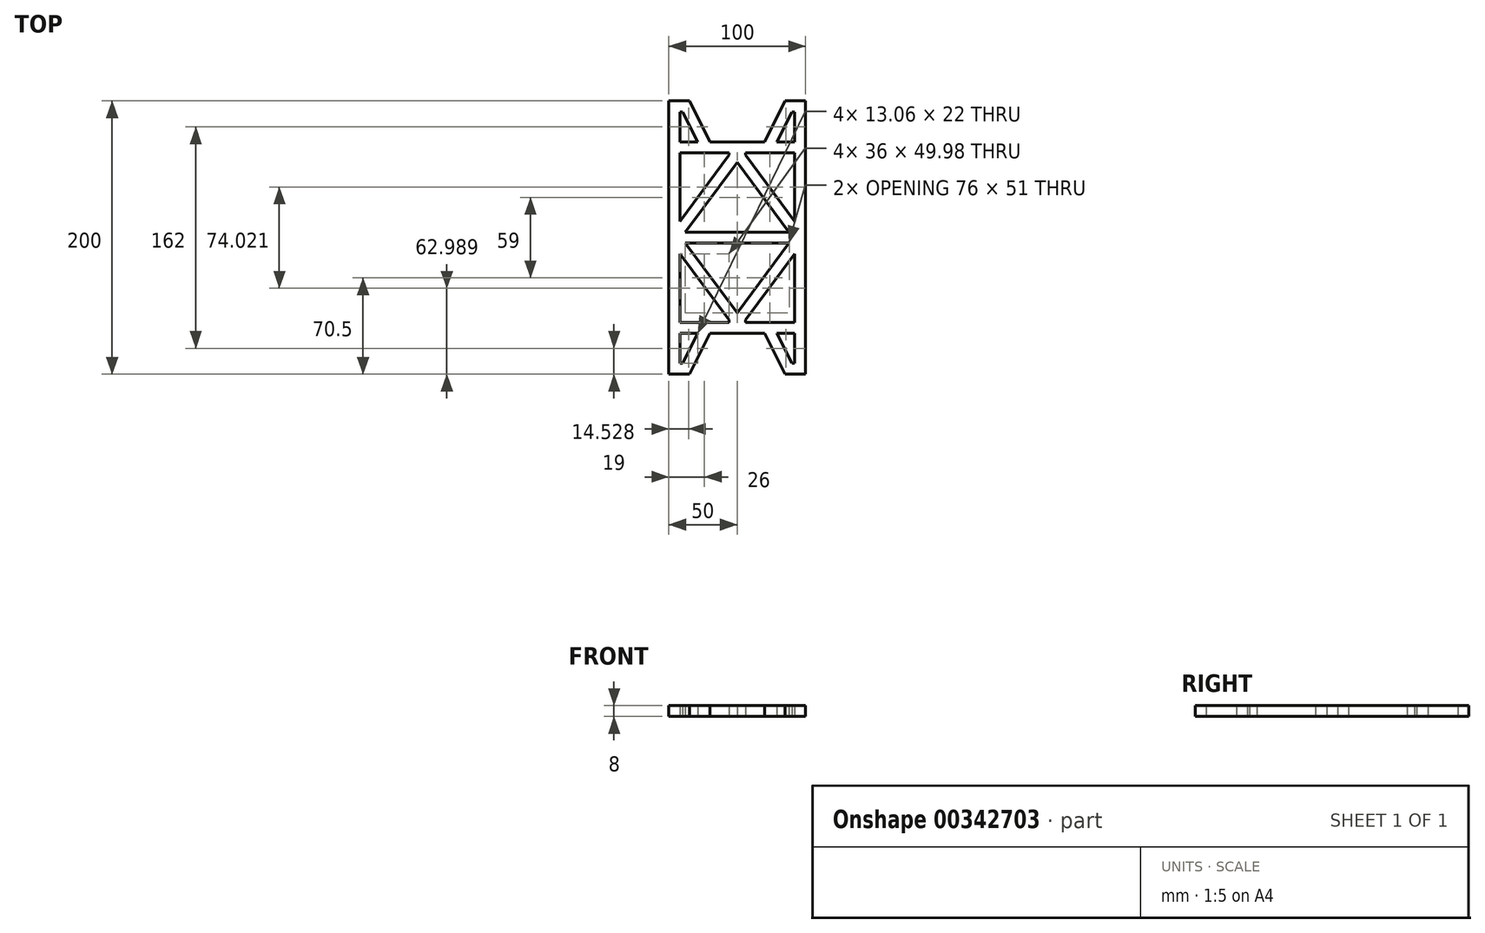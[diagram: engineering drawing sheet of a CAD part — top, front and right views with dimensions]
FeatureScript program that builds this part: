
annotation { "Feature Type Name" : "Feature", "Feature Type Description" : "" }
export const myFeature = defineFeature(function(context is Context, id is Id, definition is map)
    precondition{}
    {
        {
            var Q0;
            Q0=qCreatedBy(makeId("Top.planeOp"),FACE);
            var sketch = newSketch(context, id + "F0", { "sketchPlane" : qUnion([Q0])});
            skLineSegment(sketch, "E0.bottom", {"start": v(-50, 100) * mm, "end": v(0, 100) * mm, "construction": true});
            skLineSegment(sketch, "E0.top", {"start": v(-50, 0) * mm, "end": v(0, 0) * mm, "construction": true});
            skLineSegment(sketch, "E0.left", {"start": v(-50, 100) * mm, "end": v(-50, 0) * mm, "construction": true});
            skLineSegment(sketch, "E0.right", {"start": v(0, 100) * mm, "end": v(0, 0) * mm, "construction": true});
            skLineSegment(sketch, "E1", {"start": v(-50, 0) * mm, "end": v(-50, 100) * mm});
            skLineSegment(sketch, "E2", {"start": v(-50, 100) * mm, "end": v(-35, 100) * mm});
            skLineSegment(sketch, "E3", {"start": v(-35, 100) * mm, "end": v(-20, 70) * mm});
            skLineSegment(sketch, "E4", {"start": v(-20, 70) * mm, "end": v(0, 70) * mm});
            skLineSegment(sketch, "E5", {"start": v(0, 70) * mm, "end": v(0, 55) * mm});
            skLineSegment(sketch, "E6", {"start": v(0, 55) * mm, "end": v(-38, 4) * mm});
            skLineSegment(sketch, "E7.0", {"start": v(-39.94, 92) * mm, "end": v(-28.94, 70) * mm});
            skLineSegment(sketch, "E7.1", {"start": v(-42, 92) * mm, "end": v(-39.94, 92) * mm});
            skLineSegment(sketch, "E7.2", {"start": v(-42, 70) * mm, "end": v(-42, 92) * mm});
            skLineSegment(sketch, "E8.0", {"start": v(-6, 60.34) * mm, "end": v(-42, 12.02) * mm});
            skLineSegment(sketch, "E9", {"start": v(-6, 60.34) * mm, "end": v(-6, 62) * mm});
            skLineSegment(sketch, "E10", {"start": v(-6, 62) * mm, "end": v(-42, 62) * mm});
            skLineSegment(sketch, "E11", {"start": v(-42, 70) * mm, "end": v(-28.94, 70) * mm});
            skLineSegment(sketch, "E12", {"start": v(-42, 62) * mm, "end": v(-42, 12.02) * mm});
            skLineSegment(sketch, "E13", {"start": v(-38, 4) * mm, "end": v(0, 4) * mm});
            skLineSegment(sketch, "E14.MirrorCS", {"start": v(-50, 0) * mm, "end": v(-50, -100) * mm});
            skLineSegment(sketch, "E15.MirrorCS", {"start": v(-50, -100) * mm, "end": v(-35, -100) * mm});
            skLineSegment(sketch, "E16.MirrorCS", {"start": v(-20, -70) * mm, "end": v(0, -70) * mm});
            skLineSegment(sketch, "E17.MirrorCS", {"start": v(-38, -4) * mm, "end": v(0, -4) * mm});
            skLineSegment(sketch, "E18.MirrorCS", {"start": v(0, -55) * mm, "end": v(-38, -4) * mm});
            skLineSegment(sketch, "E19.MirrorCS", {"start": v(-42, -92) * mm, "end": v(-39.94, -92) * mm});
            skLineSegment(sketch, "E20.MirrorCS", {"start": v(-6, -60.34) * mm, "end": v(-6, -62) * mm});
            skLineSegment(sketch, "E21.MirrorCS", {"start": v(-6, -60.34) * mm, "end": v(-42, -12.02) * mm});
            skLineSegment(sketch, "E22.MirrorCS", {"start": v(-42, -70) * mm, "end": v(-28.94, -70) * mm});
            skLineSegment(sketch, "E23.MirrorCS", {"start": v(-6, -62) * mm, "end": v(-42, -62) * mm});
            skLineSegment(sketch, "E24.MirrorCS", {"start": v(-42, -70) * mm, "end": v(-42, -92) * mm});
            skLineSegment(sketch, "E25.MirrorCS", {"start": v(-39.94, -92) * mm, "end": v(-28.94, -70) * mm});
            skLineSegment(sketch, "E26.MirrorCS", {"start": v(-35, -100) * mm, "end": v(-20, -70) * mm});
            skLineSegment(sketch, "E27.MirrorCS", {"start": v(-42, -62) * mm, "end": v(-42, -12.02) * mm});
            skLineSegment(sketch, "E28.MirrorCS", {"start": v(42, -92) * mm, "end": v(39.94, -92) * mm});
            skLineSegment(sketch, "E29.MirrorCS", {"start": v(6, -60.34) * mm, "end": v(6, -62) * mm});
            skLineSegment(sketch, "E30.MirrorCS", {"start": v(6, -60.34) * mm, "end": v(42, -12.02) * mm});
            skLineSegment(sketch, "E31.MirrorCS", {"start": v(50, 0) * mm, "end": v(50, -100) * mm});
            skLineSegment(sketch, "E32.MirrorCS", {"start": v(42, -70) * mm, "end": v(28.94, -70) * mm});
            skLineSegment(sketch, "E33.MirrorCS", {"start": v(0, -55) * mm, "end": v(38, -4) * mm});
            skLineSegment(sketch, "E34.MirrorCS", {"start": v(50, -100) * mm, "end": v(35, -100) * mm});
            skLineSegment(sketch, "E35.MirrorCS", {"start": v(42, -70) * mm, "end": v(42, -92) * mm});
            skLineSegment(sketch, "E36.MirrorCS", {"start": v(42, -62) * mm, "end": v(42, -12.02) * mm});
            skLineSegment(sketch, "E37.MirrorCS", {"start": v(35, -100) * mm, "end": v(20, -70) * mm});
            skLineSegment(sketch, "E38.MirrorCS", {"start": v(38, -4) * mm, "end": v(0, -4) * mm});
            skLineSegment(sketch, "E39.MirrorCS", {"start": v(6, -62) * mm, "end": v(42, -62) * mm});
            skLineSegment(sketch, "E40.MirrorCS", {"start": v(20, -70) * mm, "end": v(0, -70) * mm});
            skLineSegment(sketch, "E41.MirrorCS", {"start": v(39.94, -92) * mm, "end": v(28.94, -70) * mm});
            skLineSegment(sketch, "E42.MirrorCS", {"start": v(6, 60.34) * mm, "end": v(6, 62) * mm});
            skLineSegment(sketch, "E43.MirrorCS", {"start": v(42, 92) * mm, "end": v(39.94, 92) * mm});
            skLineSegment(sketch, "E44.MirrorCS", {"start": v(35, 100) * mm, "end": v(20, 70) * mm});
            skLineSegment(sketch, "E45.MirrorCS", {"start": v(38, 4) * mm, "end": v(0, 4) * mm});
            skLineSegment(sketch, "E46.MirrorCS", {"start": v(50, 100) * mm, "end": v(35, 100) * mm});
            skLineSegment(sketch, "E47.MirrorCS", {"start": v(42, 70) * mm, "end": v(28.94, 70) * mm});
            skLineSegment(sketch, "E48.MirrorCS", {"start": v(39.94, 92) * mm, "end": v(28.94, 70) * mm});
            skLineSegment(sketch, "E49.MirrorCS", {"start": v(0, 55) * mm, "end": v(38, 4) * mm});
            skLineSegment(sketch, "E50.MirrorCS", {"start": v(42, 70) * mm, "end": v(42, 92) * mm});
            skLineSegment(sketch, "E51.MirrorCS", {"start": v(6, 62) * mm, "end": v(42, 62) * mm});
            skLineSegment(sketch, "E52.MirrorCS", {"start": v(20, 70) * mm, "end": v(0, 70) * mm});
            skLineSegment(sketch, "E53.MirrorCS", {"start": v(6, 60.34) * mm, "end": v(42, 12.02) * mm});
            skLineSegment(sketch, "E54.MirrorCS", {"start": v(42, 62) * mm, "end": v(42, 12.02) * mm});
            skLineSegment(sketch, "E55.MirrorCS", {"start": v(50, 0) * mm, "end": v(50, 100) * mm});
            skSolve(sketch);
        }
        {
            var Q0;
            Q0=makeQuery(id+"F0.imprint","IMPRINT",FACE,{"disambiguationData":[TD([[makeQuery(id+"F0.imprint","IMPRINT",EDGE,{"derivedFrom":sQuery(id+"F0.wireOp",EDGE,"E1")}),-1.0]])]});
            extrude(context, id + "F1", {"entities" : qUnion([Q0]), "depth" : 8 * mm});
        }
    });
